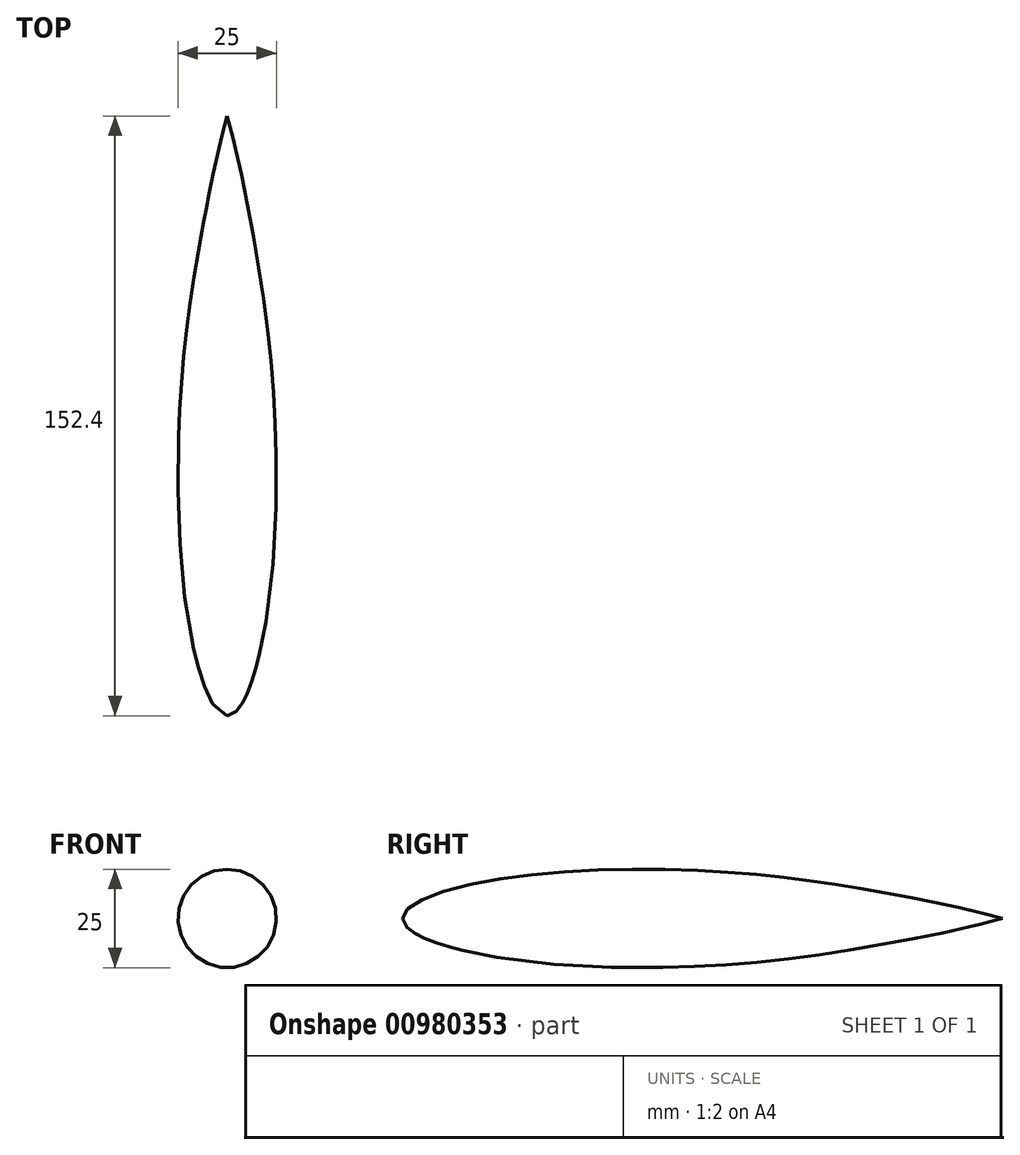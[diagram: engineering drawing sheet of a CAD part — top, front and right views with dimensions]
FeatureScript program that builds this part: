
annotation { "Feature Type Name" : "Feature", "Feature Type Description" : "" }
export const myFeature = defineFeature(function(context is Context, id is Id, definition is map)
    precondition{}
    {
        {
            var Q0;
            Q0=qCreatedBy(makeId("Right.planeOp"),FACE);
            var sketch = newSketch(context, id + "F0", { "sketchPlane" : qUnion([Q0])});
            skLineSegment(sketch, "E0", {"start": v(0, 0) * mm, "end": v(-76.2, 0) * mm});
            skLineSegment(sketch, "E1", {"start": v(0, 0) * mm, "end": v(76.2, 0) * mm});
            skFitSpline(sketch, "E2", {"points": [v(-76.2, 0) * mm, v(-55.57, 9.3) * mm, v(4.21, 11.88) * mm, v(44.07, 6.9) * mm, v(76.2, 0) * mm], "startDerivative": vector(0, 58.26) * mm, "endDerivative": vector(119.26, -34.22) * mm});
            skSolve(sketch);
        }
        {
            var Q0;
            Q0 = qSketchRegion(id + "F0", true);
            var Q1;
            Q1=sQuery(id+"F0.wireOp",EDGE,"E0");
            revolve(context, id + "F1", {"surfaceOperationType" : NewSurfaceOperationType.NEW, "entities" : qUnion([Q0]), "axis" : qUnion([Q1]), "revolveType" : RevolveType.FULL});
        }
    });
